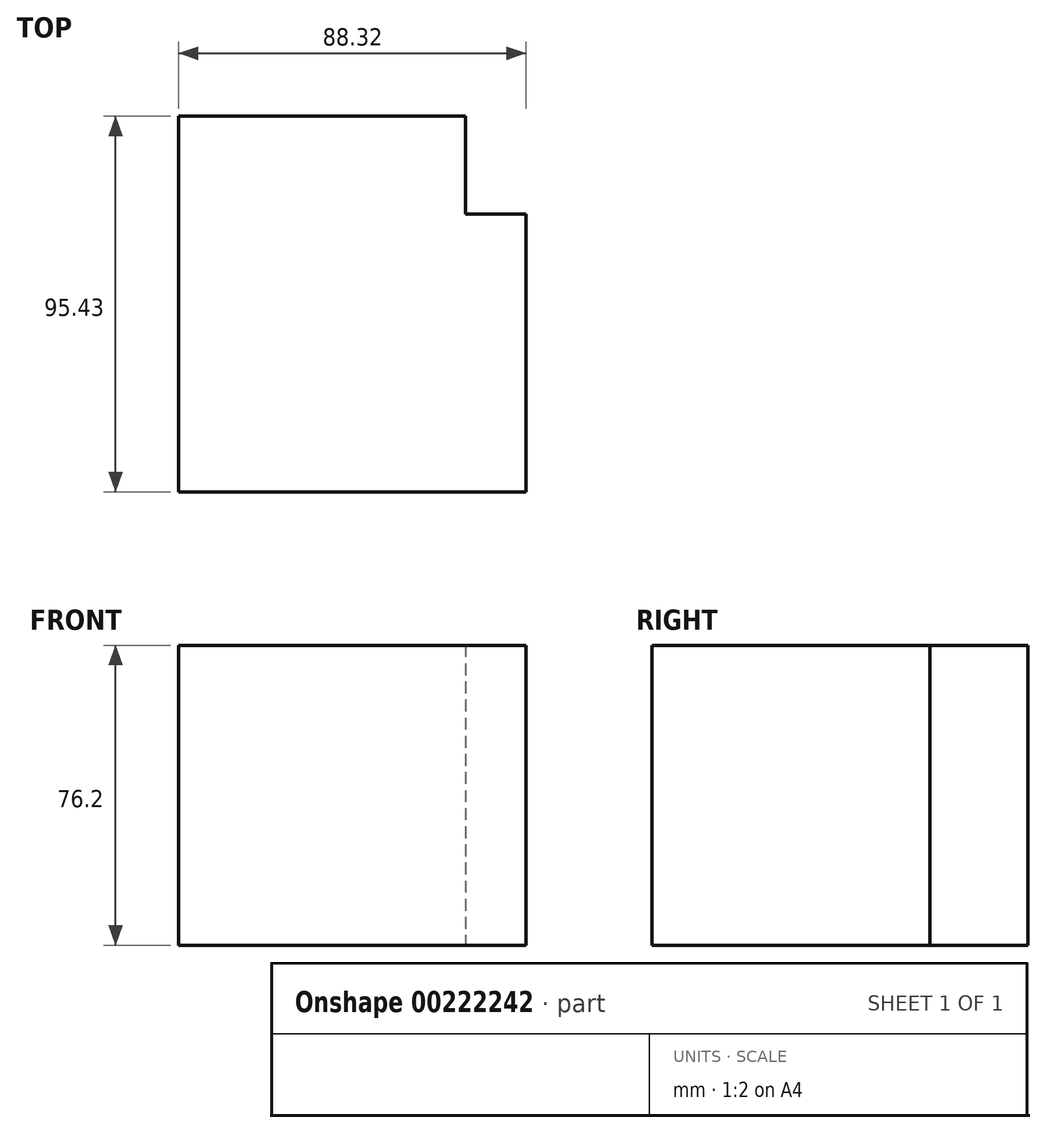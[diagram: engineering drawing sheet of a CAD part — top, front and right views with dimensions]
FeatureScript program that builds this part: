
annotation { "Feature Type Name" : "Feature", "Feature Type Description" : "" }
export const myFeature = defineFeature(function(context is Context, id is Id, definition is map)
    precondition{}
    {
        {
            var Q0;
            Q0=qCreatedBy(makeId("Top.planeOp"),FACE);
            var sketch = newSketch(context, id + "F0", { "sketchPlane" : qUnion([Q0])});
            skLineSegment(sketch, "E0.bottom", {"start": v(-72.9, -70.54) * mm, "end": v(15.4, -70.54) * mm});
            skLineSegment(sketch, "E0.top", {"start": v(-72.9, 24.9) * mm, "end": v(15.4, 24.9) * mm});
            skLineSegment(sketch, "E0.left", {"start": v(-72.9, -70.54) * mm, "end": v(-72.9, 24.9) * mm});
            skLineSegment(sketch, "E0.right", {"start": v(15.4, -70.54) * mm, "end": v(15.4, 24.9) * mm});
            skLineSegment(sketch, "E1.bottom", {"start": v(15.4, 24.9) * mm, "end": v(0, 24.9) * mm});
            skLineSegment(sketch, "E1.top", {"start": v(15.4, 0) * mm, "end": v(0, 0) * mm});
            skLineSegment(sketch, "E1.left", {"start": v(15.4, 24.9) * mm, "end": v(15.4, 0) * mm});
            skLineSegment(sketch, "E1.right", {"start": v(0, 24.9) * mm, "end": v(0, 0) * mm});
            skSolve(sketch);
        }
        {
            var Q0;
            Q0=makeQuery(id+"F0.imprint","IMPRINT",FACE,{"disambiguationData":[TD([[makeQuery(id+"F0.imprint","IMPRINT",EDGE,{"derivedFrom":sQuery(id+"F0.wireOp",EDGE,"E0.bottom")}),1.0]])]});
            extrude(context, id + "F1", {"entities" : qUnion([Q0]), "depth" : 76.2 * mm});
        }
    });
